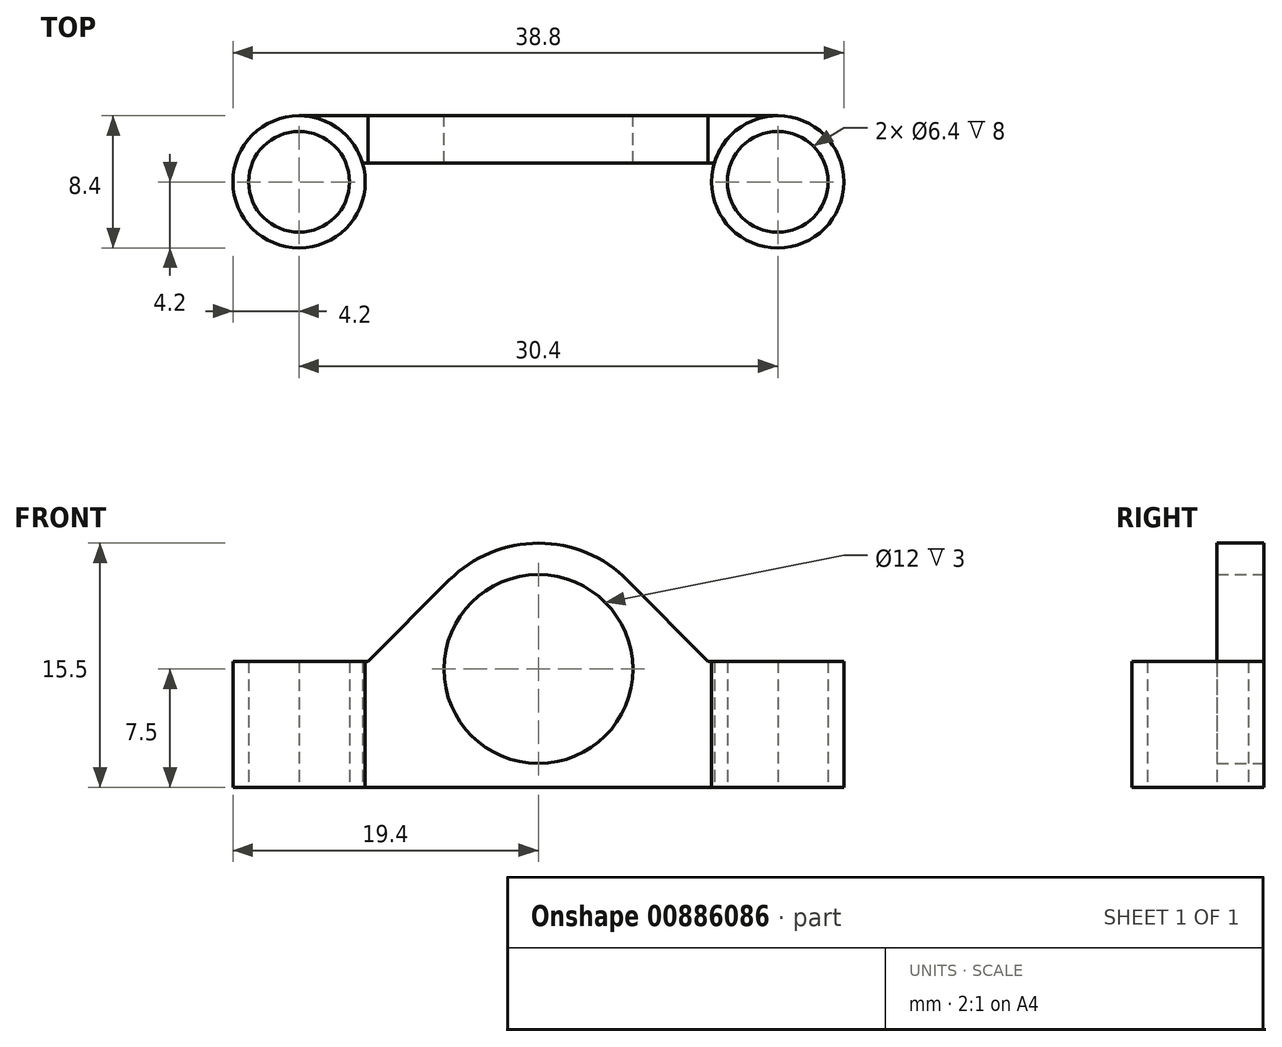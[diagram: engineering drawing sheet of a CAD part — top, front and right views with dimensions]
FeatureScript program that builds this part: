
annotation { "Feature Type Name" : "Feature", "Feature Type Description" : "" }
export const myFeature = defineFeature(function(context is Context, id is Id, definition is map)
    precondition{}
    {
        {
            var Q0;
            Q0=qCreatedBy(makeId("Top.planeOp"),FACE);
            var sketch = newSketch(context, id + "F0", { "sketchPlane" : qUnion([Q0])});
            skLineSegment(sketch, "E0.top", {"start": v(15.2, 4.2) * mm, "end": v(-15.2, 4.2) * mm});
            skPoint(sketch, "E0.middle", {"position": v(0, 0) * mm});
            skPoint(sketch, "E1", {"position": v(-15.2, 0) * mm});
            skPoint(sketch, "E2", {"position": v(15.2, 0) * mm});
            skCircle(sketch, "E3", {"center": v(-15.2, 0) * mm, "radius": 4.2 * mm});
            skCircle(sketch, "E4", {"center": v(15.2, 0) * mm, "radius": 4.2 * mm});
            skPoint(sketch, "E5.orphan", {"position": v(-19.4, 4.2) * mm});
            skPoint(sketch, "E6.orphan", {"position": v(-20, -4.2) * mm});
            skPoint(sketch, "E7.orphan", {"position": v(20, 4.2) * mm});
            skPoint(sketch, "E8.orphan", {"position": v(19.4, -4.2) * mm});
            skLineSegment(sketch, "E9", {"start": v(-11.18, 1.2) * mm, "end": v(11.18, 1.2) * mm});
            skCircle(sketch, "E10", {"center": v(-15.2, 0) * mm, "radius": 3.2 * mm});
            skCircle(sketch, "E11", {"center": v(15.2, 0) * mm, "radius": 3.2 * mm});
            skSolve(sketch);
        }
        {
            var Q0;
            Q0=makeQuery(id+"F0.imprint","IMPRINT",FACE,{"disambiguationData":[TD([[makeQuery(id+"F0.imprint","IMPRINT",EDGE,{"derivedFrom":sQuery(id+"F0.wireOp",EDGE,"E10")}),-1.0]])]});
            var Q1;
            Q1=makeQuery(id+"F0.imprint","IMPRINT",FACE,{"disambiguationData":[TD([[makeQuery(id+"F0.imprint","IMPRINT",EDGE,{"derivedFrom":sQuery(id+"F0.wireOp",EDGE,"E11")}),-1.0]])]});
            extrude(context, id + "F1", {"entities" : qUnion([Q0, Q1]), "depth" : 8 * mm, "offsetDistance" : 25 * mm});
        }
        {
            var Q0;
            {var subQ0=sQuery(id+"F0.wireOp",EDGE,"E0.top");Q0=makeQuery(id+"F0.imprint","IMPRINT",FACE,{"disambiguationData":[TD([[makeQuery(id+"F0.imprint","IMPRINT",EDGE,{"derivedFrom":subQ0}),1.0]])]});}
            extrude(context, id + "F2", {"entities" : qUnion([Q0]), "depth" : 8 * mm, "offsetDistance" : 25 * mm});
        }
        {
            var Q0;
            Q0=makeQuery(id+"F2.opExtrude","SWEPT_FACE",FACE,{"disambiguationData":[OSD([sQuery(id+"F0.wireOp",EDGE,"E0.top")])]});
            var sketch = newSketch(context, id + "F3", { "sketchPlane" : qUnion([Q0])});
            skPoint(sketch, "E12", {"position": v(0, 7.5) * mm});
            skCircle(sketch, "E13", {"center": v(0, 7.5) * mm, "radius": 6 * mm});
            skArc(sketch, "E14", {"start": v(5.66, 13.15) * mm, "mid": v(0, 15.5) * mm, "end": v(-5.67, 13.14) * mm});
            skLineSegment(sketch, "E15", {"start": v(-5.67, 13.14) * mm, "end": v(-10.78, 8) * mm});
            skLineSegment(sketch, "E16", {"start": v(5.66, 13.15) * mm, "end": v(10.8, 8) * mm});
            skLineSegment(sketch, "E17", {"start": v(-10.78, 8) * mm, "end": v(-7.92, 8.64) * mm});
            skLineSegment(sketch, "E18.trimOffspring", {"start": v(6.67, 11.92) * mm, "end": v(10.8, 8) * mm});
            skSolve(sketch);
        }
        {
            var Q0;
            Q0=makeQuery(id+"F3.imprint","IMPRINT",FACE,{"disambiguationData":[TD([[makeQuery(id+"F3.imprint","IMPRINT",EDGE,{"derivedFrom":sQuery(id+"F3.wireOp",EDGE,"E14")}),1.0]])]});
            extrude(context, id + "F4", {"entities" : qUnion([Q0]), "operationType" : NewBodyOperationType.ADD, "oppositeDirection" : true, "depth" : 3 * mm, "offsetDistance" : 25 * mm});
        }
        {
            var Q0;
            {var subQ0=sQuery(id+"F3.wireOp",EDGE,"E13");var subQ1=makeQuery(id+"F2.opExtrude","CAP_EDGE",EDGE,{"disambiguationData":[OSD([sQuery(id+"F0.wireOp",EDGE,"E0.top")])],"isStart":false});var subQ2=makeQuery(id+"F3.imprint","INTERSECT",VERTEX,{"disambiguationData":[OD(0.0)],"derivedFrom":[subQ1,subQ0]});Q0=makeQuery(id+"F3.imprint","IMPRINT",FACE,{"disambiguationData":[TD([[makeQuery(id+"F3.imprint","IMPRINT",EDGE,{"disambiguationData":[TD([[subQ2,-1.0]])],"derivedFrom":subQ0}),1.0]])]});}
            extrude(context, id + "F5", {"entities" : qUnion([Q0]), "operationType" : NewBodyOperationType.REMOVE, "oppositeDirection" : true, "depth" : 3 * mm, "offsetDistance" : 25 * mm});
        }
    });
